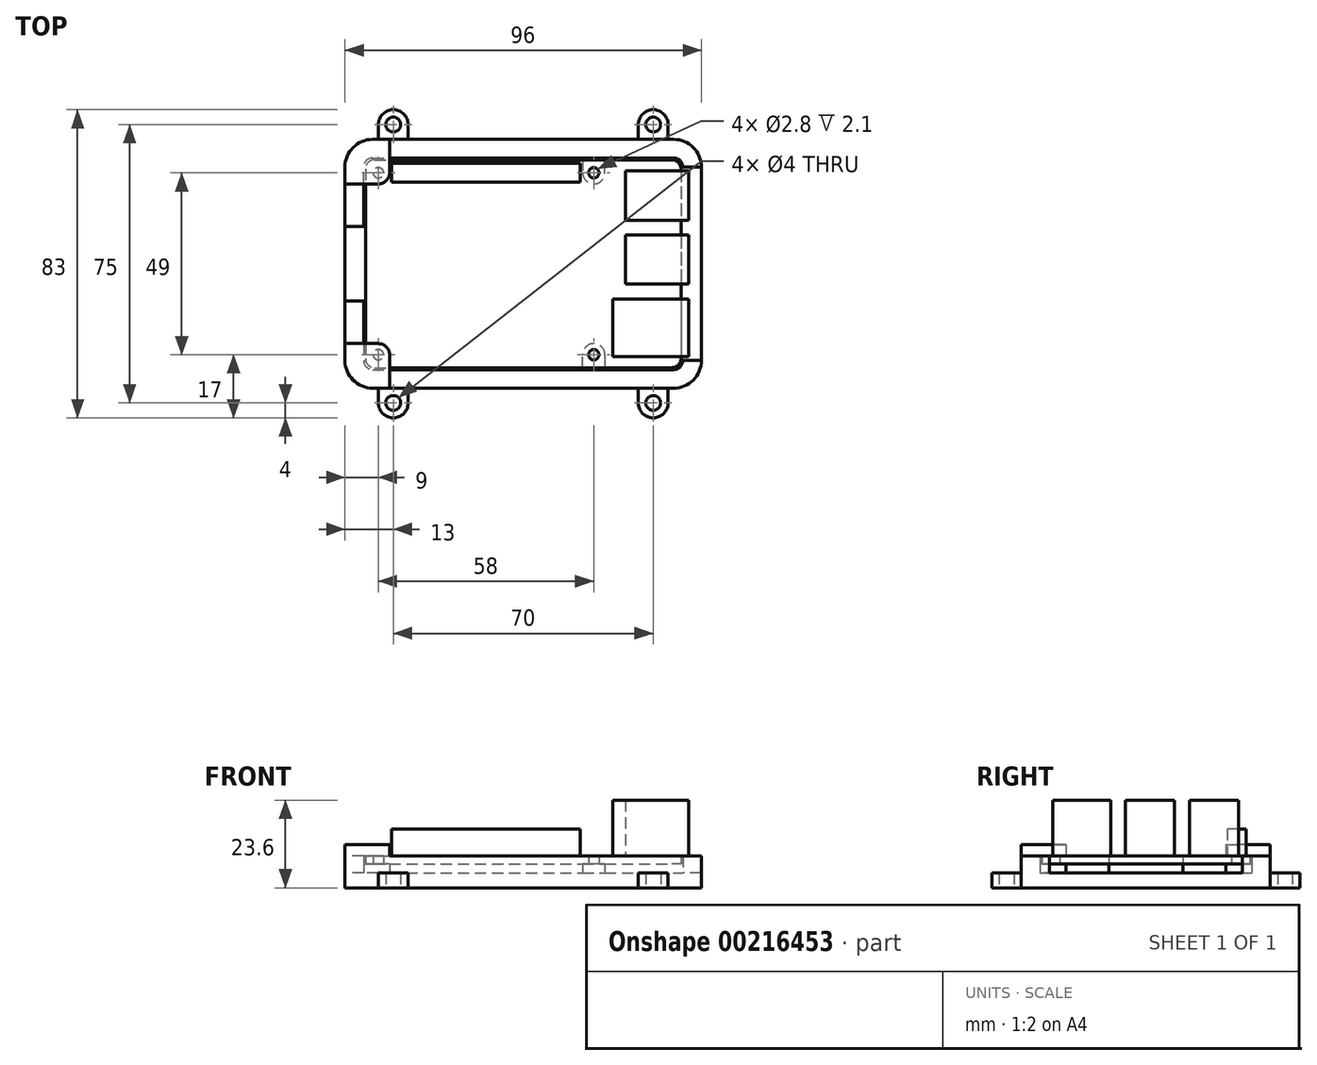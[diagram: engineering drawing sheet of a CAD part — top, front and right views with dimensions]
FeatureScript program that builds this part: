
annotation { "Feature Type Name" : "Feature", "Feature Type Description" : "" }
export const myFeature = defineFeature(function(context is Context, id is Id, definition is map)
    precondition{}
    {
        {
            var Q0;
            Q0=qCreatedBy(makeId("Top.planeOp"),FACE);
            var sketch = newSketch(context, id + "F0", { "sketchPlane" : qUnion([Q0])});
            skLineSegment(sketch, "E0.bottom", {"start": v(-40, 28) * mm, "end": v(40, 28) * mm});
            skLineSegment(sketch, "E0.top", {"start": v(-40, -28) * mm, "end": v(40, -28) * mm});
            skLineSegment(sketch, "E0.left", {"start": v(-42.5, 25.5) * mm, "end": v(-42.5, -25.5) * mm});
            skLineSegment(sketch, "E0.right", {"start": v(42.5, 25.5) * mm, "end": v(42.5, -25.5) * mm});
            skPoint(sketch, "E1", {"position": v(0, 28) * mm});
            skPoint(sketch, "E2", {"position": v(-42.5, 0) * mm});
            skCircle(sketch, "E3", {"center": v(-39, 24.5) * mm, "radius": 1.4 * mm});
            skCircle(sketch, "E4", {"center": v(19, 24.5) * mm, "radius": 1.4 * mm});
            skCircle(sketch, "E5", {"center": v(19, -24.5) * mm, "radius": 1.4 * mm});
            skCircle(sketch, "E6", {"center": v(-39, -24.5) * mm, "radius": 1.4 * mm});
            skLineSegment(sketch, "E7", {"start": v(-39, 24.5) * mm, "end": v(-39, -24.5) * mm, "construction": true});
            skPoint(sketch, "E8", {"position": v(-39, 0) * mm});
            skPoint(sketch, "E9.visualSharp", {"position": v(-42.5, 28) * mm});
            skArc(sketch, "E9.filletArc", {"start": v(-40, 28) * mm, "mid": v(-41.77, 27.27) * mm, "end": v(-42.5, 25.5) * mm});
            skPoint(sketch, "E10.visualSharp", {"position": v(-42.5, -28) * mm});
            skArc(sketch, "E10.filletArc", {"start": v(-42.5, -25.5) * mm, "mid": v(-41.77, -27.27) * mm, "end": v(-40, -28) * mm});
            skPoint(sketch, "E11.visualSharp", {"position": v(42.5, -28) * mm});
            skArc(sketch, "E11.filletArc", {"start": v(40, -28) * mm, "mid": v(41.77, -27.27) * mm, "end": v(42.5, -25.5) * mm});
            skPoint(sketch, "E12.visualSharp", {"position": v(42.5, 28) * mm});
            skArc(sketch, "E12.filletArc", {"start": v(42.5, 25.5) * mm, "mid": v(41.77, 27.27) * mm, "end": v(40, 28) * mm});
            skSolve(sketch);
        }
        {
            var Q0;
            Q0 = qSketchRegion(id + "F0", true);
            extrude(context, id + "F1", {"entities" : qUnion([Q0]), "depth" : 2.1 * mm});
        }
        {
            var Q0;
            Q0=makeQuery(id+"F1.opExtrude","CAP_FACE",FACE,{"disambiguationData":[OSD([sQuery(id+"F0.wireOp",EDGE,"E0.bottom"),sQuery(id+"F0.wireOp",EDGE,"E0.top"),sQuery(id+"F0.wireOp",EDGE,"E0.left"),sQuery(id+"F0.wireOp",EDGE,"E0.right"),sQuery(id+"F0.wireOp",EDGE,"E3"),sQuery(id+"F0.wireOp",EDGE,"E4"),sQuery(id+"F0.wireOp",EDGE,"E5"),sQuery(id+"F0.wireOp",EDGE,"E6"),sQuery(id+"F0.wireOp",EDGE,"E9.filletArc"),sQuery(id+"F0.wireOp",EDGE,"E10.filletArc"),sQuery(id+"F0.wireOp",EDGE,"E11.filletArc"),sQuery(id+"F0.wireOp",EDGE,"E12.filletArc")])],"isStart":false});
            var sketch = newSketch(context, id + "F2", { "sketchPlane" : qUnion([Q0])});
            skLineSegment(sketch, "E13.bottom", {"start": v(-35.4, 27.04) * mm, "end": v(15.4, 27.04) * mm});
            skLineSegment(sketch, "E13.top", {"start": v(-35.4, 21.96) * mm, "end": v(15.4, 21.96) * mm});
            skLineSegment(sketch, "E13.left", {"start": v(-35.4, 27.04) * mm, "end": v(-35.4, 21.96) * mm});
            skLineSegment(sketch, "E13.right", {"start": v(15.4, 27.04) * mm, "end": v(15.4, 21.96) * mm});
            skPoint(sketch, "E14", {"position": v(-39, 24.5) * mm});
            skPoint(sketch, "E15", {"position": v(-35.4, 24.5) * mm});
            skPoint(sketch, "E16", {"position": v(-10, 21.96) * mm});
            skLineSegment(sketch, "E17", {"start": v(-39, 24.5) * mm, "end": v(19, 24.5) * mm, "construction": true});
            skPoint(sketch, "E18", {"position": v(-10, 24.5) * mm});
            skSolve(sketch);
        }
        {
            var Q0;
            Q0 = qSketchRegion(id + "F2", true);
            extrude(context, id + "F3", {"entities" : qUnion([Q0]), "operationType" : NewBodyOperationType.ADD, "depth" : 7.2 * mm});
        }
        {
            var Q0;
            Q0=makeQuery(id+"F1.opExtrude","CAP_FACE",FACE,{"disambiguationData":[OSD([sQuery(id+"F0.wireOp",EDGE,"E0.bottom"),sQuery(id+"F0.wireOp",EDGE,"E0.top"),sQuery(id+"F0.wireOp",EDGE,"E0.left"),sQuery(id+"F0.wireOp",EDGE,"E0.right"),sQuery(id+"F0.wireOp",EDGE,"E3"),sQuery(id+"F0.wireOp",EDGE,"E4"),sQuery(id+"F0.wireOp",EDGE,"E5"),sQuery(id+"F0.wireOp",EDGE,"E6"),sQuery(id+"F0.wireOp",EDGE,"E9.filletArc"),sQuery(id+"F0.wireOp",EDGE,"E10.filletArc"),sQuery(id+"F0.wireOp",EDGE,"E11.filletArc"),sQuery(id+"F0.wireOp",EDGE,"E12.filletArc")])],"isStart":false});
            var sketch = newSketch(context, id + "F4", { "sketchPlane" : qUnion([Q0])});
            skLineSegment(sketch, "E19.bottom", {"start": v(27.6, 25) * mm, "end": v(44.6, 25) * mm});
            skLineSegment(sketch, "E19.top", {"start": v(27.6, 11.75) * mm, "end": v(44.6, 11.75) * mm});
            skLineSegment(sketch, "E19.left", {"start": v(27.6, 25) * mm, "end": v(27.6, 11.75) * mm});
            skLineSegment(sketch, "E19.right", {"start": v(44.6, 25) * mm, "end": v(44.6, 11.75) * mm});
            skLineSegment(sketch, "E20.bottom", {"start": v(27.6, 7.75) * mm, "end": v(44.6, 7.75) * mm});
            skLineSegment(sketch, "E20.top", {"start": v(27.6, -5.5) * mm, "end": v(44.6, -5.5) * mm});
            skLineSegment(sketch, "E20.left", {"start": v(27.6, 7.75) * mm, "end": v(27.6, -5.5) * mm});
            skLineSegment(sketch, "E20.right", {"start": v(44.6, 7.75) * mm, "end": v(44.6, -5.5) * mm});
            skLineSegment(sketch, "E21.bottom", {"start": v(24.1, -9.5) * mm, "end": v(44.6, -9.5) * mm});
            skLineSegment(sketch, "E21.top", {"start": v(24.1, -25) * mm, "end": v(44.6, -25) * mm});
            skLineSegment(sketch, "E21.left", {"start": v(24.1, -9.5) * mm, "end": v(24.1, -25) * mm});
            skLineSegment(sketch, "E21.right", {"start": v(44.6, -9.5) * mm, "end": v(44.6, -25) * mm});
            skLineSegment(sketch, "E22", {"start": v(27.6, 25) * mm, "end": v(27.6, 28) * mm, "construction": true});
            skLineSegment(sketch, "E23", {"start": v(24.1, -25) * mm, "end": v(24.1, -28) * mm, "construction": true});
            skSolve(sketch);
        }
        {
            var Q0;
            Q0 = qSketchRegion(id + "F4", true);
            extrude(context, id + "F5", {"entities" : qUnion([Q0]), "operationType" : NewBodyOperationType.ADD, "depth" : 15 * mm});
        }
        {
            var Q0;
            Q0=qCreatedBy(makeId("Top.planeOp"),FACE);
            cPlane(context, id + "F6", {"entities" : qUnion([Q0]), "cplaneType" : CPlaneType.OFFSET, "offset" : 2.5 * mm, "oppositeDirection" : true, "width" : 150 * mm, "height" : 150 * mm});
        }
        {
            var Q0;
            Q0=qCreatedBy(id+"F6.planeOp",FACE);
            var sketch = newSketch(context, id + "F7", { "sketchPlane" : qUnion([Q0])});
            skLineSegment(sketch, "E24.bottom", {"start": v(-40.5, 28.5) * mm, "end": v(40.5, 28.5) * mm});
            skLineSegment(sketch, "E24.top", {"start": v(-40.5, -28.5) * mm, "end": v(40.5, -28.5) * mm});
            skLineSegment(sketch, "E24.left", {"start": v(-43, 26) * mm, "end": v(-43, 10) * mm});
            skLineSegment(sketch, "E24.right", {"start": v(43, 26) * mm, "end": v(43, -26) * mm});
            skPoint(sketch, "E25.visualSharp", {"position": v(-43, 28.5) * mm});
            skArc(sketch, "E25.filletArc", {"start": v(-40.5, 28.5) * mm, "mid": v(-42.27, 27.77) * mm, "end": v(-43, 26) * mm});
            skPoint(sketch, "E26.visualSharp", {"position": v(43, 28.5) * mm});
            skArc(sketch, "E26.filletArc", {"start": v(43, 26) * mm, "mid": v(42.27, 27.77) * mm, "end": v(40.5, 28.5) * mm});
            skPoint(sketch, "E27.visualSharp", {"position": v(43, -28.5) * mm});
            skArc(sketch, "E27.filletArc", {"start": v(40.5, -28.5) * mm, "mid": v(42.27, -27.77) * mm, "end": v(43, -26) * mm});
            skPoint(sketch, "E28.visualSharp", {"position": v(-43, -28.5) * mm});
            skArc(sketch, "E28.filletArc", {"start": v(-43, -26) * mm, "mid": v(-42.27, -27.77) * mm, "end": v(-40.5, -28.5) * mm});
            skLineSegment(sketch, "E29.bottom", {"start": v(-40.5, 33.5) * mm, "end": v(40.5, 33.5) * mm});
            skLineSegment(sketch, "E29.top", {"start": v(-40.5, -33.5) * mm, "end": v(40.5, -33.5) * mm});
            skLineSegment(sketch, "E29.left", {"start": v(-48, 26) * mm, "end": v(-48, 10) * mm});
            skLineSegment(sketch, "E29.right", {"start": v(48, 26) * mm, "end": v(48, -26) * mm});
            skLineSegment(sketch, "E30", {"start": v(0, 28.5) * mm, "end": v(0, 33.5) * mm, "construction": true});
            skLineSegment(sketch, "E31", {"start": v(-43, 0) * mm, "end": v(-48, 0) * mm, "construction": true});
            skLineSegment(sketch, "E32", {"start": v(0, 28.5) * mm, "end": v(0, 28) * mm, "construction": true});
            skLineSegment(sketch, "E33", {"start": v(-43, 0) * mm, "end": v(-42.5, 0) * mm, "construction": true});
            skPoint(sketch, "E34.visualSharp", {"position": v(-48, 33.5) * mm});
            skArc(sketch, "E34.filletArc", {"start": v(-40.5, 33.5) * mm, "mid": v(-45.8, 31.3) * mm, "end": v(-48, 26) * mm});
            skPoint(sketch, "E35.visualSharp", {"position": v(48, 33.5) * mm});
            skArc(sketch, "E35.filletArc", {"start": v(48, 26) * mm, "mid": v(45.8, 31.3) * mm, "end": v(40.5, 33.5) * mm});
            skPoint(sketch, "E36.visualSharp", {"position": v(48, -33.5) * mm});
            skArc(sketch, "E36.filletArc", {"start": v(40.5, -33.5) * mm, "mid": v(45.8, -31.3) * mm, "end": v(48, -26) * mm});
            skPoint(sketch, "E37.visualSharp", {"position": v(-48, -33.5) * mm});
            skArc(sketch, "E37.filletArc", {"start": v(-48, -26) * mm, "mid": v(-45.8, -31.3) * mm, "end": v(-40.5, -33.5) * mm});
            skLineSegment(sketch, "E38", {"start": v(-48, 10) * mm, "end": v(-48, -10) * mm, "construction": true});
            skLineSegment(sketch, "E39", {"start": v(-43, 10) * mm, "end": v(-43, -10) * mm, "construction": true});
            skLineSegment(sketch, "E40", {"start": v(-48, 10) * mm, "end": v(-43, 10) * mm});
            skLineSegment(sketch, "E41", {"start": v(-48, -10) * mm, "end": v(-48, -26) * mm});
            skLineSegment(sketch, "E42", {"start": v(-43, -10) * mm, "end": v(-43, -26) * mm});
            skLineSegment(sketch, "E43", {"start": v(-43, -10) * mm, "end": v(-48, -10) * mm});
            skSolve(sketch);
        }
        {
            var Q0;
            Q0 = qSketchRegion(id + "F7", true);
            var Q1;
            Q1=makeQuery(id+"F1.opExtrude","CAP_FACE",FACE,{"disambiguationData":[OSD([sQuery(id+"F0.wireOp",EDGE,"E0.bottom"),sQuery(id+"F0.wireOp",EDGE,"E0.top"),sQuery(id+"F0.wireOp",EDGE,"E0.left"),sQuery(id+"F0.wireOp",EDGE,"E0.right"),sQuery(id+"F0.wireOp",EDGE,"E3"),sQuery(id+"F0.wireOp",EDGE,"E4"),sQuery(id+"F0.wireOp",EDGE,"E5"),sQuery(id+"F0.wireOp",EDGE,"E6"),sQuery(id+"F0.wireOp",EDGE,"E9.filletArc"),sQuery(id+"F0.wireOp",EDGE,"E10.filletArc"),sQuery(id+"F0.wireOp",EDGE,"E11.filletArc"),sQuery(id+"F0.wireOp",EDGE,"E12.filletArc")])],"isStart":false});
            extrude(context, id + "F8", {"entities" : qUnion([Q0]), "endBound" : BoundingType.UP_TO_SURFACE, "endBoundEntityFace" : qUnion([Q1]), "depth" : 25 * mm});
        }
        {
            var Q0;
            Q0=qCreatedBy(id+"F6.planeOp",FACE);
            var sketch = newSketch(context, id + "F9", { "sketchPlane" : qUnion([Q0])});
            skArc(sketch, "E44", {"start": v(22, -24.5) * mm, "mid": v(19, -21.5) * mm, "end": v(16, -24.5) * mm});
            skLineSegment(sketch, "E45", {"start": v(22, -24.5) * mm, "end": v(22, -28.5) * mm});
            skLineSegment(sketch, "E46", {"start": v(22, -28.5) * mm, "end": v(16, -28.5) * mm});
            skLineSegment(sketch, "E47", {"start": v(16, -28.5) * mm, "end": v(16, -24.5) * mm});
            skLineSegment(sketch, "E48.MirrorCS", {"start": v(16, 28.5) * mm, "end": v(16, 24.5) * mm});
            skLineSegment(sketch, "E49.MirrorCS", {"start": v(22, 28.5) * mm, "end": v(16, 28.5) * mm});
            skLineSegment(sketch, "E50.MirrorCS", {"start": v(22, 24.5) * mm, "end": v(22, 28.5) * mm});
            skArc(sketch, "E51.MirrorCS", {"start": v(22, 24.5) * mm, "mid": v(19, 21.5) * mm, "end": v(16, 24.5) * mm});
            skArc(sketch, "E52", {"start": v(-39, 21.5) * mm, "mid": v(-36.88, 22.38) * mm, "end": v(-36, 24.5) * mm});
            skLineSegment(sketch, "E53", {"start": v(-36, 24.5) * mm, "end": v(-36, 28.5) * mm});
            skLineSegment(sketch, "E54", {"start": v(-39, 21.5) * mm, "end": v(-43, 21.5) * mm});
            skLineSegment(sketch, "E55", {"start": v(-43, 21.5) * mm, "end": v(-43, 28.5) * mm});
            skLineSegment(sketch, "E56", {"start": v(-43, 28.5) * mm, "end": v(-36, 28.5) * mm});
            skArc(sketch, "E57.MirrorCS", {"start": v(-39, -21.5) * mm, "mid": v(-36.88, -22.38) * mm, "end": v(-36, -24.5) * mm});
            skLineSegment(sketch, "E58.MirrorCS", {"start": v(-36, -24.5) * mm, "end": v(-36, -28.5) * mm});
            skLineSegment(sketch, "E59.MirrorCS", {"start": v(-43, -28.5) * mm, "end": v(-36, -28.5) * mm});
            skLineSegment(sketch, "E60.MirrorCS", {"start": v(-43, -21.5) * mm, "end": v(-43, -28.5) * mm});
            skLineSegment(sketch, "E61.MirrorCS", {"start": v(-39, -21.5) * mm, "end": v(-43, -21.5) * mm});
            skSolve(sketch);
        }
        {
            var Q0;
            Q0 = qSketchRegion(id + "F9", true);
            var Q1;
            Q1=qCreatedBy(makeId("Top.planeOp"),FACE);
            extrude(context, id + "F10", {"entities" : qUnion([Q0]), "operationType" : NewBodyOperationType.ADD, "endBound" : BoundingType.UP_TO_SURFACE, "endBoundEntityFace" : qUnion([Q1]), "depth" : 25 * mm});
        }
        {
            var Q0;
            Q0=qCreatedBy(id+"F6.planeOp",FACE);
            var sketch = newSketch(context, id + "F11", { "sketchPlane" : qUnion([Q0])});
            skLineSegment(sketch, "E62.bottom", {"start": v(-40.5, -33.5) * mm, "end": v(40.5, -33.5) * mm});
            skLineSegment(sketch, "E62.top", {"start": v(-40.5, 33.5) * mm, "end": v(40.5, 33.5) * mm});
            skLineSegment(sketch, "E62.left", {"start": v(-48, -26) * mm, "end": v(-48, 26) * mm});
            skLineSegment(sketch, "E62.right", {"start": v(48, -26) * mm, "end": v(48, 26) * mm});
            skPoint(sketch, "E63.visualSharp", {"position": v(-48, -33.5) * mm});
            skArc(sketch, "E63.filletArc", {"start": v(-48, -26) * mm, "mid": v(-45.8, -31.3) * mm, "end": v(-40.5, -33.5) * mm});
            skPoint(sketch, "E64.visualSharp", {"position": v(48, -33.5) * mm});
            skArc(sketch, "E64.filletArc", {"start": v(40.5, -33.5) * mm, "mid": v(45.8, -31.3) * mm, "end": v(48, -26) * mm});
            skPoint(sketch, "E65.visualSharp", {"position": v(48, 33.5) * mm});
            skArc(sketch, "E65.filletArc", {"start": v(48, 26) * mm, "mid": v(45.8, 31.3) * mm, "end": v(40.5, 33.5) * mm});
            skPoint(sketch, "E66.visualSharp", {"position": v(-48, 33.5) * mm});
            skArc(sketch, "E66.filletArc", {"start": v(-40.5, 33.5) * mm, "mid": v(-45.8, 31.3) * mm, "end": v(-48, 26) * mm});
            skSolve(sketch);
        }
        {
            var Q0;
            Q0 = qSketchRegion(id + "F11", true);
            extrude(context, id + "F12", {"entities" : qUnion([Q0]), "operationType" : NewBodyOperationType.ADD, "oppositeDirection" : true, "depth" : 4 * mm});
        }
        {
            var Q0;
            Q0=makeQuery(id+"F1.opExtrude","CAP_FACE",FACE,{"disambiguationData":[OSD([sQuery(id+"F0.wireOp",EDGE,"E0.bottom"),sQuery(id+"F0.wireOp",EDGE,"E0.top"),sQuery(id+"F0.wireOp",EDGE,"E0.left"),sQuery(id+"F0.wireOp",EDGE,"E0.right"),sQuery(id+"F0.wireOp",EDGE,"E3"),sQuery(id+"F0.wireOp",EDGE,"E4"),sQuery(id+"F0.wireOp",EDGE,"E5"),sQuery(id+"F0.wireOp",EDGE,"E6"),sQuery(id+"F0.wireOp",EDGE,"E9.filletArc"),sQuery(id+"F0.wireOp",EDGE,"E10.filletArc"),sQuery(id+"F0.wireOp",EDGE,"E11.filletArc"),sQuery(id+"F0.wireOp",EDGE,"E12.filletArc")])],"isStart":false});
            var sketch = newSketch(context, id + "F13", { "sketchPlane" : qUnion([Q0])});
            skLineSegment(sketch, "E67.bottom", {"start": v(43, 26) * mm, "end": v(75.54, 26) * mm});
            skLineSegment(sketch, "E67.top", {"start": v(43, -26) * mm, "end": v(75.54, -26) * mm});
            skLineSegment(sketch, "E67.left", {"start": v(43, 26) * mm, "end": v(43, -26) * mm});
            skLineSegment(sketch, "E67.right", {"start": v(75.54, 26) * mm, "end": v(75.54, -26) * mm});
            skPoint(sketch, "E68", {"position": v(43, 0) * mm});
            skSolve(sketch);
        }
        {
            var Q0;
            Q0 = qSketchRegion(id + "F13", true);
            var Q1;
            Q1=makeQuery(id+"F12.opExtrude","CAP_FACE",FACE,{"disambiguationData":[OSD([sQuery(id+"F11.wireOp",EDGE,"E62.bottom"),sQuery(id+"F11.wireOp",EDGE,"E62.top"),sQuery(id+"F11.wireOp",EDGE,"E62.left"),sQuery(id+"F11.wireOp",EDGE,"E62.right"),sQuery(id+"F11.wireOp",EDGE,"E63.filletArc"),sQuery(id+"F11.wireOp",EDGE,"E64.filletArc"),sQuery(id+"F11.wireOp",EDGE,"E65.filletArc"),sQuery(id+"F11.wireOp",EDGE,"E66.filletArc")])],"isStart":true});
            extrude(context, id + "F14", {"entities" : qUnion([Q0]), "operationType" : NewBodyOperationType.REMOVE, "endBound" : BoundingType.UP_TO_SURFACE, "oppositeDirection" : true, "endBoundEntityFace" : qUnion([Q1]), "depth" : 2 * mm});
        }
        {
            var Q0;
            Q0=makeQuery(id+"F1.opExtrude","CAP_FACE",FACE,{"disambiguationData":[OSD([sQuery(id+"F0.wireOp",EDGE,"E0.bottom"),sQuery(id+"F0.wireOp",EDGE,"E0.top"),sQuery(id+"F0.wireOp",EDGE,"E0.left"),sQuery(id+"F0.wireOp",EDGE,"E0.right"),sQuery(id+"F0.wireOp",EDGE,"E3"),sQuery(id+"F0.wireOp",EDGE,"E4"),sQuery(id+"F0.wireOp",EDGE,"E5"),sQuery(id+"F0.wireOp",EDGE,"E6"),sQuery(id+"F0.wireOp",EDGE,"E9.filletArc"),sQuery(id+"F0.wireOp",EDGE,"E10.filletArc"),sQuery(id+"F0.wireOp",EDGE,"E11.filletArc"),sQuery(id+"F0.wireOp",EDGE,"E12.filletArc")])],"isStart":false});
            var sketch = newSketch(context, id + "F15", { "sketchPlane" : qUnion([Q0])});
            skArc(sketch, "E69", {"start": v(-40.5, 33.5) * mm, "mid": v(-45.8, 31.3) * mm, "end": v(-48, 26) * mm});
            skLineSegment(sketch, "E70", {"start": v(-40.5, 33.5) * mm, "end": v(-36, 33.5) * mm});
            skLineSegment(sketch, "E71", {"start": v(-36, 33.5) * mm, "end": v(-36, 24.5) * mm});
            skLineSegment(sketch, "E72", {"start": v(-39, 21.5) * mm, "end": v(-48, 21.5) * mm});
            skLineSegment(sketch, "E73", {"start": v(-48, 21.5) * mm, "end": v(-48, 26) * mm});
            skPoint(sketch, "E74", {"position": v(-39, 24.5) * mm});
            skPoint(sketch, "E75.visualSharp", {"position": v(-36, 21.5) * mm});
            skArc(sketch, "E75.filletArc", {"start": v(-39, 21.5) * mm, "mid": v(-36.88, 22.38) * mm, "end": v(-36, 24.5) * mm});
            skLineSegment(sketch, "E76.bottom", {"start": v(16, 33.5) * mm, "end": v(22, 33.5) * mm, "construction": true});
            skLineSegment(sketch, "E76.top", {"start": v(18, 21.5) * mm, "end": v(20, 21.5) * mm, "construction": true});
            skLineSegment(sketch, "E76.left", {"start": v(16, 33.5) * mm, "end": v(16, 23.5) * mm, "construction": true});
            skLineSegment(sketch, "E76.right", {"start": v(22, 33.5) * mm, "end": v(22, 23.5) * mm, "construction": true});
            skPoint(sketch, "E77.visualSharp", {"position": v(16, 21.5) * mm});
            skArc(sketch, "E77.filletArc", {"start": v(16, 23.5) * mm, "mid": v(16.59, 22.09) * mm, "end": v(18, 21.5) * mm, "construction": true});
            skPoint(sketch, "E78.visualSharp", {"position": v(22, 21.5) * mm});
            skArc(sketch, "E78.filletArc", {"start": v(20, 21.5) * mm, "mid": v(21.41, 22.09) * mm, "end": v(22, 23.5) * mm, "construction": true});
            skPoint(sketch, "E79", {"position": v(19, 21.5) * mm});
            skPoint(sketch, "E80", {"position": v(19, 24.5) * mm});
            skArc(sketch, "E81.MirrorCS", {"start": v(-39, -21.5) * mm, "mid": v(-36.88, -22.38) * mm, "end": v(-36, -24.5) * mm});
            skPoint(sketch, "E82.MirrorP", {"position": v(-36, -21.5) * mm});
            skArc(sketch, "E83.MirrorCS", {"start": v(-40.5, -33.5) * mm, "mid": v(-45.8, -31.3) * mm, "end": v(-48, -26) * mm});
            skLineSegment(sketch, "E84.MirrorCS", {"start": v(-39, -21.5) * mm, "end": v(-48, -21.5) * mm});
            skLineSegment(sketch, "E85.MirrorCS", {"start": v(-36, -33.5) * mm, "end": v(-36, -24.5) * mm});
            skLineSegment(sketch, "E86.MirrorCS", {"start": v(-40.5, -33.5) * mm, "end": v(-36, -33.5) * mm});
            skLineSegment(sketch, "E87.MirrorCS", {"start": v(-48, -21.5) * mm, "end": v(-48, -26) * mm});
            skSolve(sketch);
        }
        {
            var Q0;
            Q0 = qSketchRegion(id + "F15", true);
            extrude(context, id + "F16", {"entities" : qUnion([Q0]), "operationType" : NewBodyOperationType.ADD, "depth" : 3 * mm});
        }
        {
            var Q0;
            Q0=makeQuery(id+"F12.opExtrude","CAP_FACE",FACE,{"disambiguationData":[OSD([sQuery(id+"F11.wireOp",EDGE,"E62.bottom"),sQuery(id+"F11.wireOp",EDGE,"E62.top"),sQuery(id+"F11.wireOp",EDGE,"E62.left"),sQuery(id+"F11.wireOp",EDGE,"E62.right"),sQuery(id+"F11.wireOp",EDGE,"E63.filletArc"),sQuery(id+"F11.wireOp",EDGE,"E64.filletArc"),sQuery(id+"F11.wireOp",EDGE,"E65.filletArc"),sQuery(id+"F11.wireOp",EDGE,"E66.filletArc")])],"isStart":false});
            var sketch = newSketch(context, id + "F17", { "sketchPlane" : qUnion([Q0])});
            skCircle(sketch, "E88", {"center": v(-35, -37.5) * mm, "radius": 2 * mm});
            skArc(sketch, "E89", {"start": v(-39, -37.5) * mm, "mid": v(-35, -41.5) * mm, "end": v(-31, -37.5) * mm});
            skLineSegment(sketch, "E90", {"start": v(-39, -37.5) * mm, "end": v(-39, -33.5) * mm});
            skLineSegment(sketch, "E91", {"start": v(-31, -33.5) * mm, "end": v(-31, -37.5) * mm});
            skPoint(sketch, "E92.MirrorP", {"position": v(48.5, 0) * mm});
            skLineSegment(sketch, "E93", {"start": v(-39, -33.5) * mm, "end": v(-31, -33.5) * mm});
            skLineSegment(sketch, "E94.MirrorCS", {"start": v(31, -33.5) * mm, "end": v(31, -37.5) * mm});
            skLineSegment(sketch, "E95.MirrorCS", {"start": v(39, -33.5) * mm, "end": v(31, -33.5) * mm});
            skLineSegment(sketch, "E96.MirrorCS", {"start": v(39, -37.5) * mm, "end": v(39, -33.5) * mm});
            skCircle(sketch, "E97.MirrorC", {"center": v(35, -37.5) * mm, "radius": 2 * mm});
            skArc(sketch, "E98.MirrorCS", {"start": v(39, -37.5) * mm, "mid": v(35, -41.5) * mm, "end": v(31, -37.5) * mm});
            skLineSegment(sketch, "E99.MirrorCS", {"start": v(31, 33.5) * mm, "end": v(31, 37.5) * mm});
            skLineSegment(sketch, "E100.MirrorCS", {"start": v(39, 37.5) * mm, "end": v(39, 33.5) * mm});
            skLineSegment(sketch, "E101.MirrorCS", {"start": v(-39, 37.5) * mm, "end": v(-39, 33.5) * mm});
            skLineSegment(sketch, "E102.MirrorCS", {"start": v(-31, 33.5) * mm, "end": v(-31, 37.5) * mm});
            skLineSegment(sketch, "E103.MirrorCS", {"start": v(-39, 33.5) * mm, "end": v(-31, 33.5) * mm});
            skLineSegment(sketch, "E104.MirrorCS", {"start": v(39, 33.5) * mm, "end": v(31, 33.5) * mm});
            skCircle(sketch, "E105.MirrorC", {"center": v(35, 37.5) * mm, "radius": 2 * mm});
            skArc(sketch, "E106.MirrorCS", {"start": v(39, 37.5) * mm, "mid": v(35, 41.5) * mm, "end": v(31, 37.5) * mm});
            skArc(sketch, "E107.MirrorCS", {"start": v(-39, 37.5) * mm, "mid": v(-35, 41.5) * mm, "end": v(-31, 37.5) * mm});
            skCircle(sketch, "E108.MirrorC", {"center": v(-35, 37.5) * mm, "radius": 2 * mm});
            skSolve(sketch);
        }
        {
            var Q0;
            Q0 = qSketchRegion(id + "F17", true);
            var Q1;
            {var subQ0=sQuery(id+"F11.wireOp",EDGE,"E66.filletArc");var subQ1=sQuery(id+"F11.wireOp",EDGE,"E65.filletArc");var subQ2=sQuery(id+"F11.wireOp",EDGE,"E64.filletArc");var subQ3=sQuery(id+"F11.wireOp",EDGE,"E63.filletArc");var subQ4=sQuery(id+"F11.wireOp",EDGE,"E62.right");var subQ5=sQuery(id+"F11.wireOp",EDGE,"E62.left");var subQ6=sQuery(id+"F11.wireOp",EDGE,"E62.top");var subQ7=sQuery(id+"F11.wireOp",EDGE,"E62.bottom");Q1=makeQuery(id+"F14.boolean.opBoolean","MERGE",FACE,{"derivedFrom":[makeQuery(id+"F12.opExtrude","CAP_FACE",FACE,{"disambiguationData":[OSD([subQ7,subQ6,subQ5,subQ4,subQ3,subQ2,subQ1,subQ0])],"isStart":true}),makeQuery(id+"F14.opExtrude","CAP_FACE",FACE,{"disambiguationData":[OSD([subQ7,subQ6,subQ5,subQ4,subQ3,subQ2,subQ1,subQ0])],"isStart":false})]});}
            extrude(context, id + "F18", {"entities" : qUnion([Q0]), "operationType" : NewBodyOperationType.ADD, "oppositeDirection" : true, "endBoundEntityFace" : qUnion([Q1]), "depth" : 4 * mm});
        }
    });
